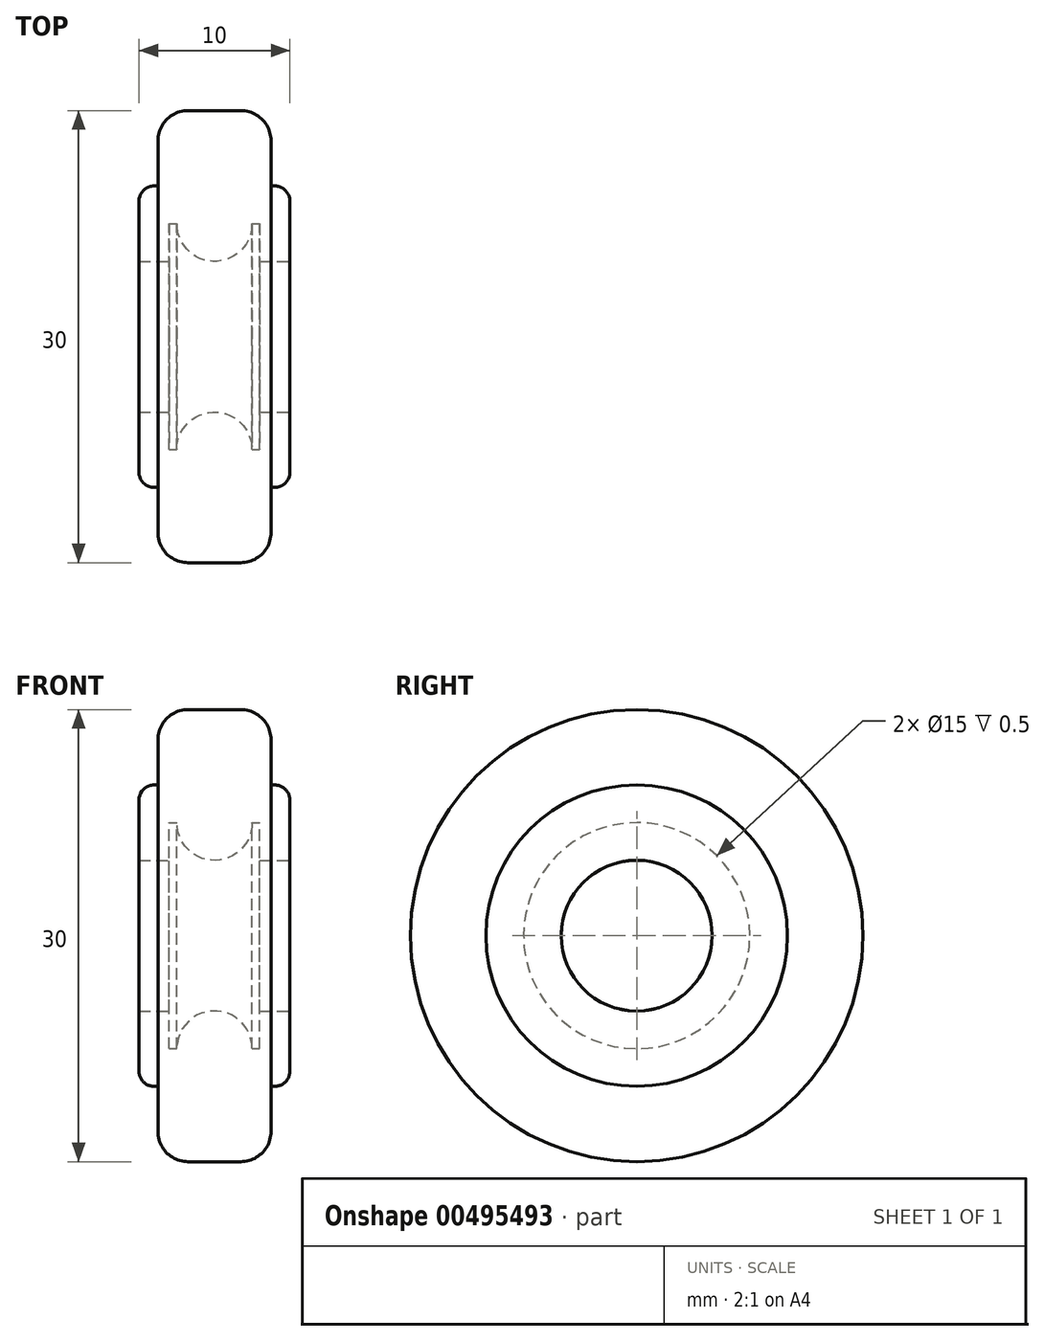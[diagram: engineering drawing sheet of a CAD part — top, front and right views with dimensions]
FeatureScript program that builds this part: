
annotation { "Feature Type Name" : "Feature", "Feature Type Description" : "" }
export const myFeature = defineFeature(function(context is Context, id is Id, definition is map)
    precondition{}
    {
        {
            var Q0;
            Q0=qCreatedBy(makeId("Front.planeOp"),FACE);
            var sketch = newSketch(context, id + "F0", { "sketchPlane" : qUnion([Q0])});
            skLineSegment(sketch, "E0", {"start": v(0, 20.14) * mm, "end": v(0, 7.5) * mm, "construction": true});
            skLineSegment(sketch, "E1", {"start": v(0, 0) * mm, "end": v(-23.8, 0) * mm, "construction": true});
            skLineSegment(sketch, "E2.bottom", {"start": v(0, 0) * mm, "end": v(-3.75, 0) * mm});
            skLineSegment(sketch, "E2.top", {"start": v(0, 15) * mm, "end": v(-1.75, 15) * mm});
            skLineSegment(sketch, "E2.right", {"start": v(-3.75, 10) * mm, "end": v(-3.75, 13) * mm});
            skLineSegment(sketch, "E3", {"start": v(-3.75, 10) * mm, "end": v(-4, 10) * mm});
            skLineSegment(sketch, "E4", {"start": v(-5, 9) * mm, "end": v(-5, 5) * mm});
            skLineSegment(sketch, "E5", {"start": v(-3.75, 10) * mm, "end": v(0, 10) * mm});
            skPoint(sketch, "E5.endSnap0", {"position": v(0, 10.07) * mm});
            skPoint(sketch, "E6.visualSharp", {"position": v(-5, 10) * mm});
            skArc(sketch, "E6.filletArc", {"start": v(-4, 10) * mm, "mid": v(-4.7, 9.7) * mm, "end": v(-5, 9) * mm});
            skLineSegment(sketch, "E7", {"start": v(-5, 5) * mm, "end": v(-3, 5) * mm});
            skPoint(sketch, "E8.orphan", {"position": v(-5, 1) * mm});
            skPoint(sketch, "E9.visualSharp", {"position": v(-3.75, 15) * mm});
            skArc(sketch, "E9.filletArc", {"start": v(-1.75, 15) * mm, "mid": v(-3.16, 14.41) * mm, "end": v(-3.75, 13) * mm});
            skLineSegment(sketch, "E10.MirrorCS", {"start": v(3.75, 10) * mm, "end": v(4, 10) * mm});
            skArc(sketch, "E11.MirrorCS", {"start": v(4, 10) * mm, "mid": v(4.7, 9.7) * mm, "end": v(5, 9) * mm});
            skLineSegment(sketch, "E12.MirrorCS", {"start": v(0, 15) * mm, "end": v(1.75, 15) * mm});
            skPoint(sketch, "E13.MirrorP", {"position": v(5, 10) * mm});
            skPoint(sketch, "E14.MirrorP", {"position": v(3.75, 15) * mm});
            skLineSegment(sketch, "E15.MirrorCS", {"start": v(3.75, 10) * mm, "end": v(3.75, 13) * mm});
            skArc(sketch, "E16.MirrorCS", {"start": v(1.75, 15) * mm, "mid": v(3.16, 14.41) * mm, "end": v(3.75, 13) * mm});
            skLineSegment(sketch, "E17.MirrorCS", {"start": v(5, 5) * mm, "end": v(3, 5) * mm});
            skLineSegment(sketch, "E18.MirrorCS", {"start": v(3.75, 10) * mm, "end": v(0, 10) * mm});
            skLineSegment(sketch, "E19.MirrorCS", {"start": v(5, 9) * mm, "end": v(5, 5) * mm});
            skLineSegment(sketch, "E20.top", {"start": v(-3, 7.5) * mm, "end": v(-2.5, 7.5) * mm});
            skLineSegment(sketch, "E20.left", {"start": v(-3, 5) * mm, "end": v(-3, 7.5) * mm});
            skLineSegment(sketch, "E21.trimOffspring", {"start": v(0, 5) * mm, "end": v(0, 0) * mm, "construction": true});
            skPoint(sketch, "E22.orphan", {"position": v(-1, 5) * mm});
            skLineSegment(sketch, "E23.MirrorCS", {"start": v(3, 7.5) * mm, "end": v(2.5, 7.5) * mm});
            skLineSegment(sketch, "E24.MirrorCS", {"start": v(3, 5) * mm, "end": v(3, 7.5) * mm});
            skPoint(sketch, "E25.orphan", {"position": v(1, 5) * mm});
            skCircle(sketch, "E26", {"center": v(0, 7.5) * mm, "radius": 2.5 * mm});
            skSolve(sketch);
        }
        {
            var Q0;
            Q0=makeQuery(id+"F0.imprint","IMPRINT",FACE,{"disambiguationData":[TD([[makeQuery(id+"F0.imprint","IMPRINT",EDGE,{"derivedFrom":sQuery(id+"F0.wireOp",EDGE,"E2.top")}),1.0]])]});
            var Q1;
            Q1=makeQuery(id+"F0.imprint","IMPRINT",FACE,{"disambiguationData":[TD([[makeQuery(id+"F0.imprint","IMPRINT",EDGE,{"derivedFrom":sQuery(id+"F0.wireOp",EDGE,"E3")}),1.0]])]});
            var Q2;
            {var subQ0=sQuery(id+"F0.wireOp",EDGE,"E26");var subQ3=makeQuery(id+"F0.imprint","INTERSECT",VERTEX,{"derivedFrom":[sQuery(id+"F0.wireOp",EDGE,"E20.top"),subQ0]});Q2=makeQuery(id+"F0.imprint","IMPRINT",FACE,{"disambiguationData":[TD([[makeQuery(id+"F0.imprint","IMPRINT",EDGE,{"disambiguationData":[TD([[subQ3,-1.0]])],"derivedFrom":subQ0}),1.0]])]});}
            var Q3;
            Q3=makeQuery(id+"F0.imprint","IMPRINT",FACE,{"disambiguationData":[TD([[makeQuery(id+"F0.imprint","IMPRINT",EDGE,{"derivedFrom":sQuery(id+"F0.wireOp",EDGE,"E10.MirrorCS")}),-1.0]])]});
            var Q4;
            Q4=sQuery(id+"F0.wireOp",EDGE,"E1");
            revolve(context, id + "F1", {"entities" : qUnion([Q0, Q1, Q2, Q3]), "axis" : qUnion([Q4]), "revolveType" : RevolveType.FULL});
        }
    });
